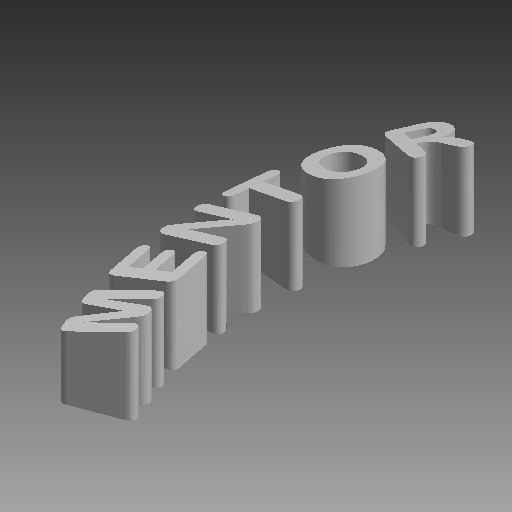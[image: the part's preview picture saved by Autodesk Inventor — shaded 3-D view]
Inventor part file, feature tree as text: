
AUTODESK INVENTOR PART (.ipt)
format: ipt  version: 2017 (Build 210142000, 142)  size: 1,180,160 bytes
history: native  units: mm (DEFAULTED — no unit token found)
features: projected_geometry x7, other x5, extrude x2, sketch x1
ambient origin geometry x8: Origin, YZ Plane, XZ Plane, XY Plane, X Axis, Y Axis, Z Axis, Center Point
bodies: Solid1 (feature_tree)
feature tree (15):
  other  "Mentor Ring.iam"
  other  "Mentor-Code ring.ipt:1"
  other  "Mentor-Mechanical ring.ipt:1"
  other  "Mentor-Electrical ring.ipt:1"
  other  "Mentor-CAD ring.ipt:1"
  extrude  "Extrusion1"  Depth=10.0mm TaperAngle=0.0deg
  extrude  "Extrusion2"  Depth=10.0mm TaperAngle=0.0deg
  projected_geometry  "Projected Loop1"
  sketch  "Sketch2"  dims[d0=10.0mm d1=10.0mm d2=0.0mm d3=0.5mm d4=0.0mm]
  projected_geometry  "Projected Loop2"
  projected_geometry  "Projected Loop3"
  projected_geometry  "Projected Loop4"
  projected_geometry  "Projected Loop5"
  projected_geometry  "Projected Loop6"
  projected_geometry  "Projected Loop7"
